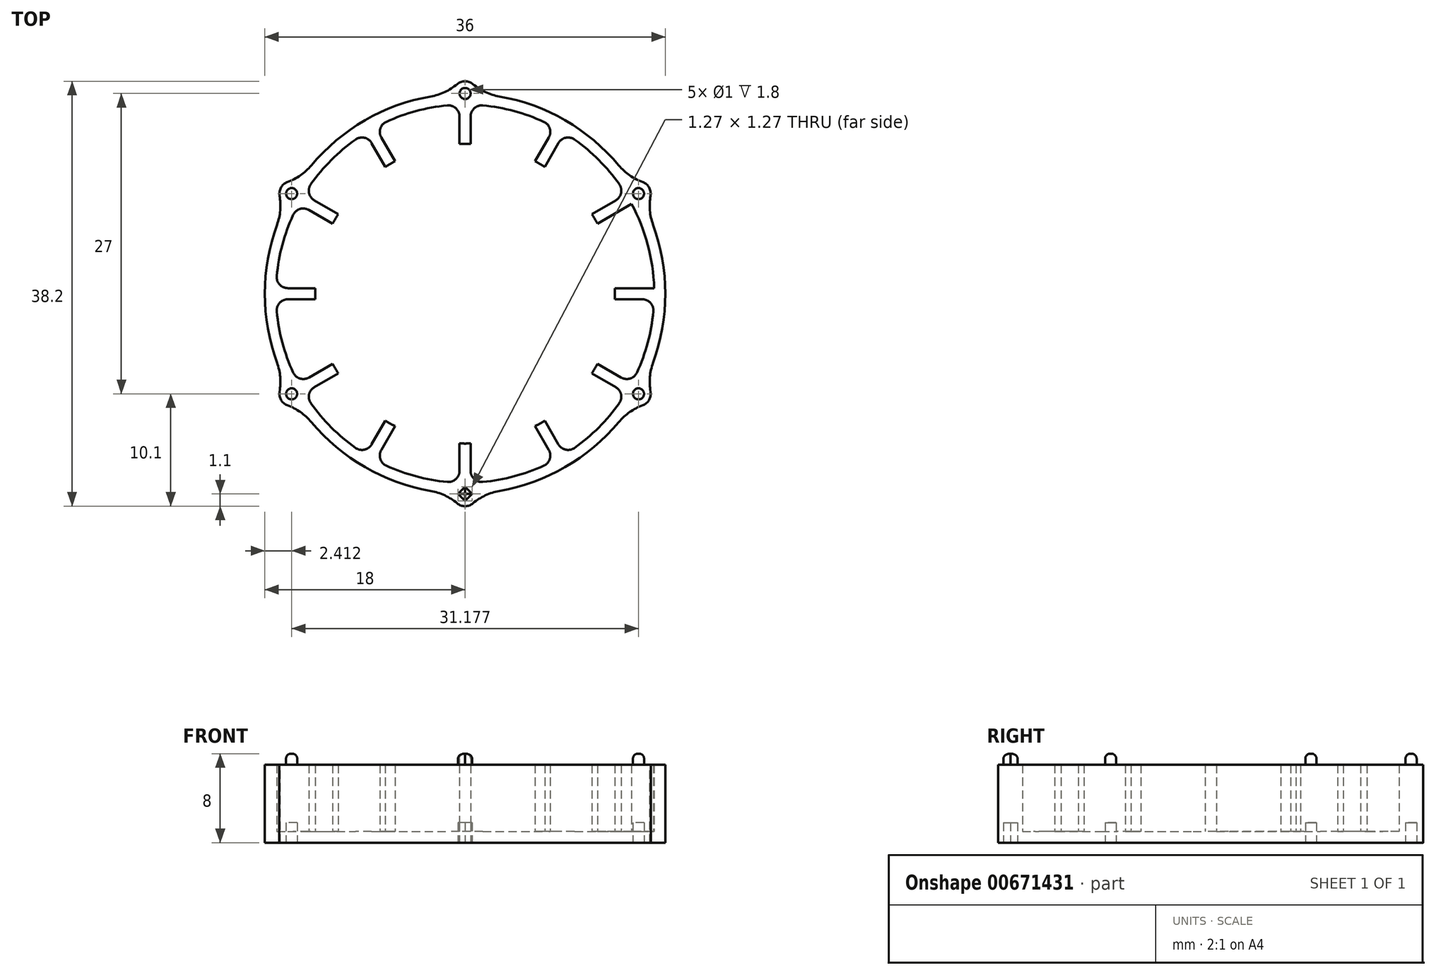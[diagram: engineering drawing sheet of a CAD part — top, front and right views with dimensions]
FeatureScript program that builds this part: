
annotation { "Feature Type Name" : "Feature", "Feature Type Description" : "" }
export const myFeature = defineFeature(function(context is Context, id is Id, definition is map)
    precondition{}
    {
        {
            var Q0;
            Q0=qCreatedBy(makeId("Top.planeOp"),FACE);
            var sketch = newSketch(context, id + "F0", { "sketchPlane" : qUnion([Q0])});
            skCircle(sketch, "E0", {"center": v(0, 0) * mm, "radius": 18 * mm});
            skCircle(sketch, "E1.0", {"center": v(0, 0) * mm, "radius": 17 * mm});
            skLineSegment(sketch, "E2.bottom", {"start": v(8.56, 15.83) * mm, "end": v(9.43, 15.33) * mm});
            skLineSegment(sketch, "E2.top", {"start": v(-9.43, -15.33) * mm, "end": v(-8.56, -15.83) * mm});
            skLineSegment(sketch, "E2.left", {"start": v(8.56, 15.83) * mm, "end": v(-9.43, -15.33) * mm});
            skLineSegment(sketch, "E2.right", {"start": v(9.43, 15.33) * mm, "end": v(-8.56, -15.83) * mm});
            skLineSegment(sketch, "E3.bottom", {"start": v(15.33, 9.43) * mm, "end": v(15.83, 8.56) * mm});
            skLineSegment(sketch, "E3.top", {"start": v(-15.83, -8.56) * mm, "end": v(-15.33, -9.43) * mm});
            skLineSegment(sketch, "E3.left", {"start": v(15.33, 9.43) * mm, "end": v(-15.83, -8.56) * mm});
            skLineSegment(sketch, "E3.right", {"start": v(15.83, 8.56) * mm, "end": v(-15.33, -9.43) * mm});
            skLineSegment(sketch, "E4", {"start": v(-38.35, 0) * mm, "end": v(39.17, 0) * mm, "construction": true});
            skLineSegment(sketch, "E5", {"start": v(0, 42.5) * mm, "end": v(0, -42.47) * mm, "construction": true});
            skLineSegment(sketch, "E6.bottom", {"start": v(-18, 0.5) * mm, "end": v(18, 0.5) * mm});
            skLineSegment(sketch, "E6.top", {"start": v(-18, -0.5) * mm, "end": v(18, -0.5) * mm});
            skLineSegment(sketch, "E6.left", {"start": v(-18, 0.5) * mm, "end": v(-18, -0.5) * mm});
            skLineSegment(sketch, "E6.right", {"start": v(18, 0.5) * mm, "end": v(18, -0.5) * mm});
            skLineSegment(sketch, "E7.bottom", {"start": v(-15.33, 9.43) * mm, "end": v(15.83, -8.56) * mm});
            skLineSegment(sketch, "E7.top", {"start": v(-15.83, 8.56) * mm, "end": v(15.33, -9.43) * mm});
            skLineSegment(sketch, "E7.left", {"start": v(-15.33, 9.43) * mm, "end": v(-15.83, 8.56) * mm});
            skLineSegment(sketch, "E7.right", {"start": v(15.83, -8.56) * mm, "end": v(15.33, -9.43) * mm});
            skLineSegment(sketch, "E8.bottom", {"start": v(-0.5, 18) * mm, "end": v(0.5, 18) * mm});
            skLineSegment(sketch, "E8.top", {"start": v(-0.5, -18) * mm, "end": v(0.5, -18) * mm});
            skLineSegment(sketch, "E8.left", {"start": v(-0.5, 18) * mm, "end": v(-0.5, -18) * mm});
            skLineSegment(sketch, "E8.right", {"start": v(0.5, 18) * mm, "end": v(0.5, -18) * mm});
            skLineSegment(sketch, "E9.bottom", {"start": v(-9.43, 15.33) * mm, "end": v(-8.56, 15.83) * mm});
            skLineSegment(sketch, "E9.top", {"start": v(8.56, -15.83) * mm, "end": v(9.43, -15.33) * mm});
            skLineSegment(sketch, "E9.left", {"start": v(-9.43, 15.33) * mm, "end": v(8.56, -15.83) * mm});
            skLineSegment(sketch, "E9.right", {"start": v(-8.56, 15.83) * mm, "end": v(9.43, -15.33) * mm});
            skCircle(sketch, "E10", {"center": v(0, 0) * mm, "radius": 13.47 * mm});
            skSolve(sketch);
        }
        {
            var Q0;
            Q0=qCreatedBy(makeId("Top.planeOp"),FACE);
            var sketch = newSketch(context, id + "F1", { "sketchPlane" : qUnion([Q0])});
            skCircle(sketch, "E11", {"center": v(0, 0) * mm, "radius": 18 * mm});
            skCircle(sketch, "E12", {"center": v(0, 0) * mm, "radius": 17 * mm});
            skSolve(sketch);
        }
        {
            var Q0;
            Q0=makeQuery(id+"F1.imprint","IMPRINT",FACE,{"disambiguationData":[TD([[makeQuery(id+"F1.imprint","IMPRINT",EDGE,{"derivedFrom":sQuery(id+"F1.wireOp",EDGE,"E11")}),1.0]])]});
            extrude(context, id + "F2", {"entities" : qUnion([Q0]), "depth" : 7 * mm, "offsetDistance" : 25 * mm});
        }
        {
            var Q0;
            {var subQ0=sQuery(id+"F0.wireOp",EDGE,"E7.bottom");var subQ1=sQuery(id+"F0.wireOp",EDGE,"E1.0");var subQ2=makeQuery(id+"F0.imprint","INTERSECT",VERTEX,{"disambiguationData":[OD(0.0)],"derivedFrom":[subQ1,subQ0]});Q0=makeQuery(id+"F0.imprint","IMPRINT",FACE,{"disambiguationData":[TD([[makeQuery(id+"F0.imprint","IMPRINT",EDGE,{"disambiguationData":[TD([[subQ2,-1.0]])],"derivedFrom":subQ1}),1.0]])]});}
            var Q1;
            {var subQ0=sQuery(id+"F0.wireOp",EDGE,"E2.right");var subQ1=sQuery(id+"F0.wireOp",EDGE,"E1.0");var subQ2=makeQuery(id+"F0.imprint","INTERSECT",VERTEX,{"disambiguationData":[OD(0.0)],"derivedFrom":[subQ1,subQ0]});Q1=makeQuery(id+"F0.imprint","IMPRINT",FACE,{"disambiguationData":[TD([[makeQuery(id+"F0.imprint","IMPRINT",EDGE,{"disambiguationData":[TD([[subQ2,-1.0]])],"derivedFrom":subQ1}),1.0]])]});}
            var Q2;
            {var subQ0=sQuery(id+"F0.wireOp",EDGE,"E6.bottom");var subQ1=sQuery(id+"F0.wireOp",EDGE,"E1.0");var subQ2=makeQuery(id+"F0.imprint","INTERSECT",VERTEX,{"disambiguationData":[OD(0.0)],"derivedFrom":[subQ1,subQ0]});Q2=makeQuery(id+"F0.imprint","IMPRINT",FACE,{"disambiguationData":[TD([[makeQuery(id+"F0.imprint","IMPRINT",EDGE,{"disambiguationData":[TD([[subQ2,1.0]])],"derivedFrom":subQ1}),1.0]])]});}
            var Q3;
            {var subQ0=sQuery(id+"F0.wireOp",EDGE,"E8.left");var subQ1=sQuery(id+"F0.wireOp",EDGE,"E1.0");var subQ2=makeQuery(id+"F0.imprint","INTERSECT",VERTEX,{"disambiguationData":[OD(1.0)],"derivedFrom":[subQ1,subQ0]});Q3=makeQuery(id+"F0.imprint","IMPRINT",FACE,{"disambiguationData":[TD([[makeQuery(id+"F0.imprint","IMPRINT",EDGE,{"disambiguationData":[TD([[subQ2,-1.0]])],"derivedFrom":subQ1}),1.0]])]});}
            var Q4;
            {var subQ0=sQuery(id+"F0.wireOp",EDGE,"E3.left");var subQ1=sQuery(id+"F0.wireOp",EDGE,"E1.0");var subQ2=makeQuery(id+"F0.imprint","INTERSECT",VERTEX,{"disambiguationData":[OD(1.0)],"derivedFrom":[subQ1,subQ0]});Q4=makeQuery(id+"F0.imprint","IMPRINT",FACE,{"disambiguationData":[TD([[makeQuery(id+"F0.imprint","IMPRINT",EDGE,{"disambiguationData":[TD([[subQ2,-1.0]])],"derivedFrom":subQ1}),1.0]])]});}
            var Q5;
            {var subQ0=sQuery(id+"F0.wireOp",EDGE,"E9.right");var subQ1=sQuery(id+"F0.wireOp",EDGE,"E1.0");var subQ2=makeQuery(id+"F0.imprint","INTERSECT",VERTEX,{"disambiguationData":[OD(0.0)],"derivedFrom":[subQ1,subQ0]});Q5=makeQuery(id+"F0.imprint","IMPRINT",FACE,{"disambiguationData":[TD([[makeQuery(id+"F0.imprint","IMPRINT",EDGE,{"disambiguationData":[TD([[subQ2,-1.0]])],"derivedFrom":subQ1}),1.0]])]});}
            var Q6;
            {var subQ0=sQuery(id+"F0.wireOp",EDGE,"E8.right");var subQ1=sQuery(id+"F0.wireOp",EDGE,"E1.0");var subQ2=makeQuery(id+"F0.imprint","INTERSECT",VERTEX,{"disambiguationData":[OD(0.0)],"derivedFrom":[subQ1,subQ0]});Q6=makeQuery(id+"F0.imprint","IMPRINT",FACE,{"disambiguationData":[TD([[makeQuery(id+"F0.imprint","IMPRINT",EDGE,{"disambiguationData":[TD([[subQ2,-1.0]])],"derivedFrom":subQ1}),1.0]])]});}
            var Q7;
            {var subQ0=sQuery(id+"F0.wireOp",EDGE,"E3.right");var subQ1=sQuery(id+"F0.wireOp",EDGE,"E1.0");var subQ2=makeQuery(id+"F0.imprint","INTERSECT",VERTEX,{"disambiguationData":[OD(0.0)],"derivedFrom":[subQ1,subQ0]});Q7=makeQuery(id+"F0.imprint","IMPRINT",FACE,{"disambiguationData":[TD([[makeQuery(id+"F0.imprint","IMPRINT",EDGE,{"disambiguationData":[TD([[subQ2,-1.0]])],"derivedFrom":subQ1}),1.0]])]});}
            var Q8;
            {var subQ0=sQuery(id+"F0.wireOp",EDGE,"E7.top");var subQ1=sQuery(id+"F0.wireOp",EDGE,"E1.0");var subQ2=makeQuery(id+"F0.imprint","INTERSECT",VERTEX,{"disambiguationData":[OD(1.0)],"derivedFrom":[subQ1,subQ0]});Q8=makeQuery(id+"F0.imprint","IMPRINT",FACE,{"disambiguationData":[TD([[makeQuery(id+"F0.imprint","IMPRINT",EDGE,{"disambiguationData":[TD([[subQ2,-1.0]])],"derivedFrom":subQ1}),1.0]])]});}
            var Q9;
            {var subQ0=sQuery(id+"F0.wireOp",EDGE,"E9.left");var subQ1=sQuery(id+"F0.wireOp",EDGE,"E1.0");var subQ2=makeQuery(id+"F0.imprint","INTERSECT",VERTEX,{"disambiguationData":[OD(1.0)],"derivedFrom":[subQ1,subQ0]});Q9=makeQuery(id+"F0.imprint","IMPRINT",FACE,{"disambiguationData":[TD([[makeQuery(id+"F0.imprint","IMPRINT",EDGE,{"disambiguationData":[TD([[subQ2,-1.0]])],"derivedFrom":subQ1}),1.0]])]});}
            var Q10;
            {var subQ0=sQuery(id+"F0.wireOp",EDGE,"E2.left");var subQ1=sQuery(id+"F0.wireOp",EDGE,"E1.0");var subQ2=makeQuery(id+"F0.imprint","INTERSECT",VERTEX,{"disambiguationData":[OD(1.0)],"derivedFrom":[subQ1,subQ0]});Q10=makeQuery(id+"F0.imprint","IMPRINT",FACE,{"disambiguationData":[TD([[makeQuery(id+"F0.imprint","IMPRINT",EDGE,{"disambiguationData":[TD([[subQ2,-1.0]])],"derivedFrom":subQ1}),1.0]])]});}
            var Q11;
            {var subQ0=sQuery(id+"F0.wireOp",EDGE,"E6.bottom");var subQ1=sQuery(id+"F0.wireOp",EDGE,"E1.0");var subQ2=makeQuery(id+"F0.imprint","INTERSECT",VERTEX,{"disambiguationData":[OD(1.0)],"derivedFrom":[subQ1,subQ0]});Q11=makeQuery(id+"F0.imprint","IMPRINT",FACE,{"disambiguationData":[TD([[makeQuery(id+"F0.imprint","IMPRINT",EDGE,{"disambiguationData":[TD([[subQ2,-1.0]])],"derivedFrom":subQ1}),1.0]])]});}
            extrude(context, id + "F3", {"entities" : qUnion([Q0, Q1, Q2, Q3, Q4, Q5, Q6, Q7, Q8, Q9, Q10, Q11]), "operationType" : NewBodyOperationType.ADD, "depth" : 7 * mm, "offsetDistance" : 25 * mm});
        }
        {
            var Q0;
            Q0=makeQuery(id+"F1.imprint","IMPRINT",FACE,{"disambiguationData":[TD([[makeQuery(id+"F1.imprint","IMPRINT",EDGE,{"derivedFrom":sQuery(id+"F1.wireOp",EDGE,"E11")}),1.0]])]});
            var Q1;
            Q1=makeQuery(id+"F1.imprint","IMPRINT",FACE,{"disambiguationData":[TD([[makeQuery(id+"F1.imprint","IMPRINT",EDGE,{"derivedFrom":sQuery(id+"F1.wireOp",EDGE,"E12")}),1.0]])]});
            extrude(context, id + "F4", {"entities" : qUnion([Q0, Q1]), "operationType" : NewBodyOperationType.ADD, "depth" : 1 * mm, "offsetDistance" : 25 * mm});
        }
        {
            var Q0;
            Q0=qCreatedBy(makeId("Top.planeOp"),FACE);
            var sketch = newSketch(context, id + "F5", { "sketchPlane" : qUnion([Q0])});
            skCircle(sketch, "E13", {"center": v(0, 0) * mm, "radius": 18 * mm});
            skLineSegment(sketch, "E14", {"start": v(0, 18) * mm, "end": v(0, -18) * mm, "construction": true});
            skLineSegment(sketch, "E15", {"start": v(15.59, 9) * mm, "end": v(0, 0) * mm, "construction": true});
            skLineSegment(sketch, "E16", {"start": v(9, 15.59) * mm, "end": v(0, 0) * mm, "construction": true});
            skLineSegment(sketch, "E17", {"start": v(0, 0) * mm, "end": v(18, 0) * mm, "construction": true});
            skLineSegment(sketch, "E18", {"start": v(0, 0) * mm, "end": v(15.59, -9) * mm, "construction": true});
            skLineSegment(sketch, "E19", {"start": v(0, 0) * mm, "end": v(9, -15.59) * mm, "construction": true});
            skLineSegment(sketch, "E20", {"start": v(0, 0) * mm, "end": v(-9, 15.59) * mm, "construction": true});
            skLineSegment(sketch, "E21", {"start": v(0, 0) * mm, "end": v(-15.59, 9) * mm, "construction": true});
            skLineSegment(sketch, "E22", {"start": v(0, 0) * mm, "end": v(-18, 0) * mm, "construction": true});
            skLineSegment(sketch, "E23", {"start": v(0, 0) * mm, "end": v(-15.59, -9) * mm, "construction": true});
            skLineSegment(sketch, "E24", {"start": v(0, 0) * mm, "end": v(-9, -15.59) * mm, "construction": true});
            skCircle(sketch, "E25", {"center": v(0, 18) * mm, "radius": 1.1 * mm});
            skCircle(sketch, "E26", {"center": v(15.59, 9) * mm, "radius": 1.1 * mm});
            skCircle(sketch, "E27", {"center": v(15.59, -9) * mm, "radius": 1.1 * mm});
            skCircle(sketch, "E28", {"center": v(0, -18) * mm, "radius": 1.1 * mm});
            skCircle(sketch, "E29", {"center": v(-15.59, -9) * mm, "radius": 1.1 * mm});
            skCircle(sketch, "E30", {"center": v(-15.59, 9) * mm, "radius": 1.1 * mm});
            skCircle(sketch, "E31", {"center": v(-15.59, 9) * mm, "radius": 0.5 * mm});
            skCircle(sketch, "E32", {"center": v(0, 18) * mm, "radius": 0.5 * mm});
            skCircle(sketch, "E33", {"center": v(15.59, 9) * mm, "radius": 0.5 * mm});
            skCircle(sketch, "E34", {"center": v(15.59, -9) * mm, "radius": 0.5 * mm});
            skCircle(sketch, "E35", {"center": v(-15.59, -9) * mm, "radius": 0.5 * mm});
            skLineSegment(sketch, "E36.bottom", {"start": v(0.64, -18) * mm, "end": v(0, -18.64) * mm});
            skLineSegment(sketch, "E36.top", {"start": v(0, -17.36) * mm, "end": v(-0.64, -18) * mm});
            skLineSegment(sketch, "E36.left", {"start": v(0.64, -18) * mm, "end": v(0, -17.36) * mm});
            skLineSegment(sketch, "E36.right", {"start": v(0, -18.64) * mm, "end": v(-0.64, -18) * mm});
            skSolve(sketch);
        }
        {
            var Q0;
            {var subQ0=sQuery(id+"F5.wireOp",EDGE,"E30");var subQ1=sQuery(id+"F5.wireOp",EDGE,"E13");var subQ2=makeQuery(id+"F5.imprint","INTERSECT",VERTEX,{"disambiguationData":[OD(0.0)],"derivedFrom":[subQ1,subQ0]});Q0=makeQuery(id+"F5.imprint","IMPRINT",FACE,{"disambiguationData":[TD([[makeQuery(id+"F5.imprint","IMPRINT",EDGE,{"disambiguationData":[TD([[subQ2,-1.0]])],"derivedFrom":subQ1}),1.0]])]});}
            var Q1;
            {var subQ0=sQuery(id+"F5.wireOp",EDGE,"E30");var subQ1=sQuery(id+"F5.wireOp",EDGE,"E13");var subQ2=makeQuery(id+"F5.imprint","INTERSECT",VERTEX,{"disambiguationData":[OD(0.0)],"derivedFrom":[subQ1,subQ0]});Q1=makeQuery(id+"F5.imprint","IMPRINT",FACE,{"disambiguationData":[TD([[makeQuery(id+"F5.imprint","IMPRINT",EDGE,{"disambiguationData":[TD([[subQ2,-1.0]])],"derivedFrom":subQ1}),-1.0]])]});}
            var Q2;
            {var subQ0=sQuery(id+"F5.wireOp",EDGE,"E25");var subQ1=sQuery(id+"F5.wireOp",EDGE,"E13");var subQ2=makeQuery(id+"F5.imprint","INTERSECT",VERTEX,{"disambiguationData":[OD(0.0)],"derivedFrom":[subQ1,subQ0]});Q2=makeQuery(id+"F5.imprint","IMPRINT",FACE,{"disambiguationData":[TD([[makeQuery(id+"F5.imprint","IMPRINT",EDGE,{"disambiguationData":[TD([[subQ2,-1.0]])],"derivedFrom":subQ1}),1.0]])]});}
            var Q3;
            {var subQ0=sQuery(id+"F5.wireOp",EDGE,"E25");var subQ1=sQuery(id+"F5.wireOp",EDGE,"E13");var subQ2=makeQuery(id+"F5.imprint","INTERSECT",VERTEX,{"disambiguationData":[OD(0.0)],"derivedFrom":[subQ1,subQ0]});Q3=makeQuery(id+"F5.imprint","IMPRINT",FACE,{"disambiguationData":[TD([[makeQuery(id+"F5.imprint","IMPRINT",EDGE,{"disambiguationData":[TD([[subQ2,-1.0]])],"derivedFrom":subQ1}),-1.0]])]});}
            var Q4;
            {var subQ0=sQuery(id+"F5.wireOp",EDGE,"E26");var subQ1=sQuery(id+"F5.wireOp",EDGE,"E13");var subQ2=makeQuery(id+"F5.imprint","INTERSECT",VERTEX,{"disambiguationData":[OD(0.0)],"derivedFrom":[subQ1,subQ0]});Q4=makeQuery(id+"F5.imprint","IMPRINT",FACE,{"disambiguationData":[TD([[makeQuery(id+"F5.imprint","IMPRINT",EDGE,{"disambiguationData":[TD([[subQ2,-1.0]])],"derivedFrom":subQ1}),-1.0]])]});}
            var Q5;
            {var subQ0=sQuery(id+"F5.wireOp",EDGE,"E26");var subQ1=sQuery(id+"F5.wireOp",EDGE,"E13");var subQ2=makeQuery(id+"F5.imprint","INTERSECT",VERTEX,{"disambiguationData":[OD(0.0)],"derivedFrom":[subQ1,subQ0]});Q5=makeQuery(id+"F5.imprint","IMPRINT",FACE,{"disambiguationData":[TD([[makeQuery(id+"F5.imprint","IMPRINT",EDGE,{"disambiguationData":[TD([[subQ2,-1.0]])],"derivedFrom":subQ1}),1.0]])]});}
            var Q6;
            {var subQ0=sQuery(id+"F5.wireOp",EDGE,"E29");var subQ1=sQuery(id+"F5.wireOp",EDGE,"E13");var subQ2=makeQuery(id+"F5.imprint","INTERSECT",VERTEX,{"disambiguationData":[OD(0.0)],"derivedFrom":[subQ1,subQ0]});Q6=makeQuery(id+"F5.imprint","IMPRINT",FACE,{"disambiguationData":[TD([[makeQuery(id+"F5.imprint","IMPRINT",EDGE,{"disambiguationData":[TD([[subQ2,-1.0]])],"derivedFrom":subQ1}),1.0]])]});}
            var Q7;
            {var subQ0=sQuery(id+"F5.wireOp",EDGE,"E29");var subQ1=sQuery(id+"F5.wireOp",EDGE,"E13");var subQ2=makeQuery(id+"F5.imprint","INTERSECT",VERTEX,{"disambiguationData":[OD(0.0)],"derivedFrom":[subQ1,subQ0]});Q7=makeQuery(id+"F5.imprint","IMPRINT",FACE,{"disambiguationData":[TD([[makeQuery(id+"F5.imprint","IMPRINT",EDGE,{"disambiguationData":[TD([[subQ2,-1.0]])],"derivedFrom":subQ1}),-1.0]])]});}
            var Q8;
            {var subQ3=sQuery(id+"F5.wireOp",EDGE,"E13");var subQ5=sQuery(id+"F5.wireOp",EDGE,"E28");var subQ6=makeQuery(id+"F5.imprint","INTERSECT",VERTEX,{"disambiguationData":[OD(0.0)],"derivedFrom":[subQ3,subQ5]});Q8=makeQuery(id+"F5.imprint","IMPRINT",FACE,{"disambiguationData":[TD([[makeQuery(id+"F5.imprint","IMPRINT",EDGE,{"disambiguationData":[TD([[subQ6,-1.0]])],"derivedFrom":subQ3}),1.0]])]});}
            var Q9;
            {var subQ6=sQuery(id+"F5.wireOp",EDGE,"E36.bottom");Q9=makeQuery(id+"F5.imprint","IMPRINT",FACE,{"disambiguationData":[TD([[makeQuery(id+"F5.imprint","IMPRINT",EDGE,{"derivedFrom":subQ6}),1.0]])]});}
            var Q10;
            {var subQ0=sQuery(id+"F5.wireOp",EDGE,"E27");var subQ1=sQuery(id+"F5.wireOp",EDGE,"E13");var subQ2=makeQuery(id+"F5.imprint","INTERSECT",VERTEX,{"disambiguationData":[OD(0.0)],"derivedFrom":[subQ1,subQ0]});Q10=makeQuery(id+"F5.imprint","IMPRINT",FACE,{"disambiguationData":[TD([[makeQuery(id+"F5.imprint","IMPRINT",EDGE,{"disambiguationData":[TD([[subQ2,-1.0]])],"derivedFrom":subQ1}),-1.0]])]});}
            var Q11;
            {var subQ0=sQuery(id+"F5.wireOp",EDGE,"E27");var subQ1=sQuery(id+"F5.wireOp",EDGE,"E13");var subQ2=makeQuery(id+"F5.imprint","INTERSECT",VERTEX,{"disambiguationData":[OD(0.0)],"derivedFrom":[subQ1,subQ0]});Q11=makeQuery(id+"F5.imprint","IMPRINT",FACE,{"disambiguationData":[TD([[makeQuery(id+"F5.imprint","IMPRINT",EDGE,{"disambiguationData":[TD([[subQ2,-1.0]])],"derivedFrom":subQ1}),1.0]])]});}
            var Q12;
            {var subQ0=sQuery(id+"F5.wireOp",EDGE,"E31");var subQ1=sQuery(id+"F5.wireOp",EDGE,"E13");var subQ2=makeQuery(id+"F5.imprint","INTERSECT",VERTEX,{"disambiguationData":[OD(0.0)],"derivedFrom":[subQ1,subQ0]});Q12=makeQuery(id+"F5.imprint","IMPRINT",FACE,{"disambiguationData":[TD([[makeQuery(id+"F5.imprint","IMPRINT",EDGE,{"disambiguationData":[TD([[subQ2,-1.0]])],"derivedFrom":subQ1}),1.0]])]});}
            var Q13;
            {var subQ0=sQuery(id+"F5.wireOp",EDGE,"E31");var subQ1=sQuery(id+"F5.wireOp",EDGE,"E13");var subQ2=makeQuery(id+"F5.imprint","INTERSECT",VERTEX,{"disambiguationData":[OD(0.0)],"derivedFrom":[subQ1,subQ0]});Q13=makeQuery(id+"F5.imprint","IMPRINT",FACE,{"disambiguationData":[TD([[makeQuery(id+"F5.imprint","IMPRINT",EDGE,{"disambiguationData":[TD([[subQ2,-1.0]])],"derivedFrom":subQ1}),-1.0]])]});}
            var Q14;
            {var subQ0=sQuery(id+"F5.wireOp",EDGE,"E32");var subQ1=sQuery(id+"F5.wireOp",EDGE,"E13");var subQ2=makeQuery(id+"F5.imprint","INTERSECT",VERTEX,{"disambiguationData":[OD(0.0)],"derivedFrom":[subQ1,subQ0]});Q14=makeQuery(id+"F5.imprint","IMPRINT",FACE,{"disambiguationData":[TD([[makeQuery(id+"F5.imprint","IMPRINT",EDGE,{"disambiguationData":[TD([[subQ2,-1.0]])],"derivedFrom":subQ1}),-1.0]])]});}
            var Q15;
            {var subQ0=sQuery(id+"F5.wireOp",EDGE,"E32");var subQ1=sQuery(id+"F5.wireOp",EDGE,"E13");var subQ2=makeQuery(id+"F5.imprint","INTERSECT",VERTEX,{"disambiguationData":[OD(0.0)],"derivedFrom":[subQ1,subQ0]});Q15=makeQuery(id+"F5.imprint","IMPRINT",FACE,{"disambiguationData":[TD([[makeQuery(id+"F5.imprint","IMPRINT",EDGE,{"disambiguationData":[TD([[subQ2,-1.0]])],"derivedFrom":subQ1}),1.0]])]});}
            var Q16;
            {var subQ0=sQuery(id+"F5.wireOp",EDGE,"E33");var subQ1=sQuery(id+"F5.wireOp",EDGE,"E13");var subQ2=makeQuery(id+"F5.imprint","INTERSECT",VERTEX,{"disambiguationData":[OD(0.0)],"derivedFrom":[subQ1,subQ0]});Q16=makeQuery(id+"F5.imprint","IMPRINT",FACE,{"disambiguationData":[TD([[makeQuery(id+"F5.imprint","IMPRINT",EDGE,{"disambiguationData":[TD([[subQ2,-1.0]])],"derivedFrom":subQ1}),-1.0]])]});}
            var Q17;
            {var subQ0=sQuery(id+"F5.wireOp",EDGE,"E33");var subQ1=sQuery(id+"F5.wireOp",EDGE,"E13");var subQ2=makeQuery(id+"F5.imprint","INTERSECT",VERTEX,{"disambiguationData":[OD(0.0)],"derivedFrom":[subQ1,subQ0]});Q17=makeQuery(id+"F5.imprint","IMPRINT",FACE,{"disambiguationData":[TD([[makeQuery(id+"F5.imprint","IMPRINT",EDGE,{"disambiguationData":[TD([[subQ2,-1.0]])],"derivedFrom":subQ1}),1.0]])]});}
            var Q18;
            {var subQ0=sQuery(id+"F5.wireOp",EDGE,"E34");var subQ1=sQuery(id+"F5.wireOp",EDGE,"E13");var subQ2=makeQuery(id+"F5.imprint","INTERSECT",VERTEX,{"disambiguationData":[OD(0.0)],"derivedFrom":[subQ1,subQ0]});Q18=makeQuery(id+"F5.imprint","IMPRINT",FACE,{"disambiguationData":[TD([[makeQuery(id+"F5.imprint","IMPRINT",EDGE,{"disambiguationData":[TD([[subQ2,-1.0]])],"derivedFrom":subQ1}),-1.0]])]});}
            var Q19;
            {var subQ0=sQuery(id+"F5.wireOp",EDGE,"E34");var subQ1=sQuery(id+"F5.wireOp",EDGE,"E13");var subQ2=makeQuery(id+"F5.imprint","INTERSECT",VERTEX,{"disambiguationData":[OD(0.0)],"derivedFrom":[subQ1,subQ0]});Q19=makeQuery(id+"F5.imprint","IMPRINT",FACE,{"disambiguationData":[TD([[makeQuery(id+"F5.imprint","IMPRINT",EDGE,{"disambiguationData":[TD([[subQ2,-1.0]])],"derivedFrom":subQ1}),1.0]])]});}
            var Q20;
            {var subQ1=sQuery(id+"F5.wireOp",EDGE,"E36.bottom");Q20=makeQuery(id+"F5.imprint","IMPRINT",FACE,{"disambiguationData":[TD([[makeQuery(id+"F5.imprint","IMPRINT",EDGE,{"derivedFrom":subQ1}),-1.0]])]});}
            var Q21;
            {var subQ0=sQuery(id+"F5.wireOp",EDGE,"E35");var subQ1=sQuery(id+"F5.wireOp",EDGE,"E13");var subQ2=makeQuery(id+"F5.imprint","INTERSECT",VERTEX,{"disambiguationData":[OD(0.0)],"derivedFrom":[subQ1,subQ0]});Q21=makeQuery(id+"F5.imprint","IMPRINT",FACE,{"disambiguationData":[TD([[makeQuery(id+"F5.imprint","IMPRINT",EDGE,{"disambiguationData":[TD([[subQ2,-1.0]])],"derivedFrom":subQ1}),-1.0]])]});}
            var Q22;
            {var subQ0=sQuery(id+"F5.wireOp",EDGE,"E35");var subQ1=sQuery(id+"F5.wireOp",EDGE,"E13");var subQ2=makeQuery(id+"F5.imprint","INTERSECT",VERTEX,{"disambiguationData":[OD(0.0)],"derivedFrom":[subQ1,subQ0]});Q22=makeQuery(id+"F5.imprint","IMPRINT",FACE,{"disambiguationData":[TD([[makeQuery(id+"F5.imprint","IMPRINT",EDGE,{"disambiguationData":[TD([[subQ2,-1.0]])],"derivedFrom":subQ1}),1.0]])]});}
            var Q23;
            {var subQ0=sQuery(id+"F5.wireOp",EDGE,"E36.top");var subQ1=sQuery(id+"F5.wireOp",EDGE,"E13");var subQ2=makeQuery(id+"F5.imprint","INTERSECT",VERTEX,{"derivedFrom":[subQ1,subQ0]});Q23=makeQuery(id+"F5.imprint","IMPRINT",FACE,{"disambiguationData":[TD([[makeQuery(id+"F5.imprint","IMPRINT",EDGE,{"disambiguationData":[TD([[subQ2,-1.0]])],"derivedFrom":subQ1}),1.0]])]});}
            extrude(context, id + "F6", {"entities" : qUnion([Q0, Q1, Q2, Q3, Q4, Q5, Q6, Q7, Q8, Q9, Q10, Q11, Q12, Q13, Q14, Q15, Q16, Q17, Q18, Q19, Q20, Q21, Q22, Q23]), "operationType" : NewBodyOperationType.ADD, "depth" : 7 * mm, "offsetDistance" : 25 * mm});
        }
        {
            var Q0;
            {var subQ0=sQuery(id+"F0.wireOp",EDGE,"E8.right");var subQ1=sQuery(id+"F0.wireOp",EDGE,"E1.0");Q0=makeQuery(id+"F3.opExtrude","SWEPT_EDGE",EDGE,{"disambiguationData":[OSD([subQ1,subQ0]),TDD([makeQuery(id+"F0.imprint","INTERSECT",VERTEX,{"disambiguationData":[OD(1.0)],"derivedFrom":[subQ1,subQ0]})])]});}
            var Q1;
            {var subQ0=sQuery(id+"F0.wireOp",EDGE,"E2.left");var subQ1=sQuery(id+"F0.wireOp",EDGE,"E1.0");Q1=makeQuery(id+"F3.opExtrude","SWEPT_EDGE",EDGE,{"disambiguationData":[OSD([subQ1,subQ0]),TDD([makeQuery(id+"F0.imprint","INTERSECT",VERTEX,{"disambiguationData":[OD(1.0)],"derivedFrom":[subQ1,subQ0]})])]});}
            var Q2;
            {var subQ0=sQuery(id+"F0.wireOp",EDGE,"E3.left");var subQ1=sQuery(id+"F0.wireOp",EDGE,"E1.0");Q2=makeQuery(id+"F3.opExtrude","SWEPT_EDGE",EDGE,{"disambiguationData":[OSD([subQ1,subQ0]),TDD([makeQuery(id+"F0.imprint","INTERSECT",VERTEX,{"disambiguationData":[OD(1.0)],"derivedFrom":[subQ1,subQ0]})])]});}
            var Q3;
            {var subQ0=sQuery(id+"F0.wireOp",EDGE,"E6.bottom");var subQ1=sQuery(id+"F0.wireOp",EDGE,"E1.0");Q3=makeQuery(id+"F3.opExtrude","SWEPT_EDGE",EDGE,{"disambiguationData":[OSD([subQ1,subQ0]),TDD([makeQuery(id+"F0.imprint","INTERSECT",VERTEX,{"disambiguationData":[OD(1.0)],"derivedFrom":[subQ1,subQ0]})])]});}
            var Q4;
            {var subQ0=sQuery(id+"F0.wireOp",EDGE,"E9.right");var subQ1=sQuery(id+"F0.wireOp",EDGE,"E1.0");Q4=makeQuery(id+"F3.opExtrude","SWEPT_EDGE",EDGE,{"disambiguationData":[OSD([subQ1,subQ0]),TDD([makeQuery(id+"F0.imprint","INTERSECT",VERTEX,{"disambiguationData":[OD(1.0)],"derivedFrom":[subQ1,subQ0]})])]});}
            var Q5;
            {var subQ0=sQuery(id+"F0.wireOp",EDGE,"E7.bottom");var subQ1=sQuery(id+"F0.wireOp",EDGE,"E1.0");Q5=makeQuery(id+"F3.opExtrude","SWEPT_EDGE",EDGE,{"disambiguationData":[OSD([subQ1,subQ0]),TDD([makeQuery(id+"F0.imprint","INTERSECT",VERTEX,{"disambiguationData":[OD(1.0)],"derivedFrom":[subQ1,subQ0]})])]});}
            var Q6;
            {var subQ0=sQuery(id+"F0.wireOp",EDGE,"E8.left");var subQ1=sQuery(id+"F0.wireOp",EDGE,"E1.0");Q6=makeQuery(id+"F3.opExtrude","SWEPT_EDGE",EDGE,{"disambiguationData":[OSD([subQ1,subQ0]),TDD([makeQuery(id+"F0.imprint","INTERSECT",VERTEX,{"disambiguationData":[OD(0.0)],"derivedFrom":[subQ1,subQ0]})])]});}
            var Q7;
            {var subQ0=sQuery(id+"F0.wireOp",EDGE,"E2.left");var subQ1=sQuery(id+"F0.wireOp",EDGE,"E1.0");Q7=makeQuery(id+"F3.opExtrude","SWEPT_EDGE",EDGE,{"disambiguationData":[OSD([subQ1,subQ0]),TDD([makeQuery(id+"F0.imprint","INTERSECT",VERTEX,{"disambiguationData":[OD(0.0)],"derivedFrom":[subQ1,subQ0]})])]});}
            var Q8;
            {var subQ0=sQuery(id+"F0.wireOp",EDGE,"E3.left");var subQ1=sQuery(id+"F0.wireOp",EDGE,"E1.0");Q8=makeQuery(id+"F3.opExtrude","SWEPT_EDGE",EDGE,{"disambiguationData":[OSD([subQ1,subQ0]),TDD([makeQuery(id+"F0.imprint","INTERSECT",VERTEX,{"disambiguationData":[OD(0.0)],"derivedFrom":[subQ1,subQ0]})])]});}
            var Q9;
            {var subQ0=sQuery(id+"F0.wireOp",EDGE,"E6.top");var subQ1=sQuery(id+"F0.wireOp",EDGE,"E1.0");Q9=makeQuery(id+"F3.opExtrude","SWEPT_EDGE",EDGE,{"disambiguationData":[OSD([subQ1,subQ0]),TDD([makeQuery(id+"F0.imprint","INTERSECT",VERTEX,{"disambiguationData":[OD(1.0)],"derivedFrom":[subQ1,subQ0]})])]});}
            var Q10;
            {var subQ0=sQuery(id+"F0.wireOp",EDGE,"E7.top");var subQ1=sQuery(id+"F0.wireOp",EDGE,"E1.0");Q10=makeQuery(id+"F3.opExtrude","SWEPT_EDGE",EDGE,{"disambiguationData":[OSD([subQ1,subQ0]),TDD([makeQuery(id+"F0.imprint","INTERSECT",VERTEX,{"disambiguationData":[OD(0.0)],"derivedFrom":[subQ1,subQ0]})])]});}
            var Q11;
            {var subQ0=sQuery(id+"F0.wireOp",EDGE,"E6.top");var subQ1=sQuery(id+"F0.wireOp",EDGE,"E1.0");Q11=makeQuery(id+"F3.opExtrude","SWEPT_EDGE",EDGE,{"disambiguationData":[OSD([subQ1,subQ0]),TDD([makeQuery(id+"F0.imprint","INTERSECT",VERTEX,{"disambiguationData":[OD(0.0)],"derivedFrom":[subQ1,subQ0]})])]});}
            var Q12;
            {var subQ0=sQuery(id+"F0.wireOp",EDGE,"E9.left");var subQ1=sQuery(id+"F0.wireOp",EDGE,"E1.0");Q12=makeQuery(id+"F3.opExtrude","SWEPT_EDGE",EDGE,{"disambiguationData":[OSD([subQ1,subQ0]),TDD([makeQuery(id+"F0.imprint","INTERSECT",VERTEX,{"disambiguationData":[OD(0.0)],"derivedFrom":[subQ1,subQ0]})])]});}
            var Q13;
            {var subQ0=sQuery(id+"F0.wireOp",EDGE,"E8.right");var subQ1=sQuery(id+"F0.wireOp",EDGE,"E1.0");Q13=makeQuery(id+"F3.opExtrude","SWEPT_EDGE",EDGE,{"disambiguationData":[OSD([subQ1,subQ0]),TDD([makeQuery(id+"F0.imprint","INTERSECT",VERTEX,{"disambiguationData":[OD(0.0)],"derivedFrom":[subQ1,subQ0]})])]});}
            var Q14;
            {var subQ0=sQuery(id+"F0.wireOp",EDGE,"E7.bottom");var subQ1=sQuery(id+"F0.wireOp",EDGE,"E1.0");Q14=makeQuery(id+"F3.opExtrude","SWEPT_EDGE",EDGE,{"disambiguationData":[OSD([subQ1,subQ0]),TDD([makeQuery(id+"F0.imprint","INTERSECT",VERTEX,{"disambiguationData":[OD(0.0)],"derivedFrom":[subQ1,subQ0]})])]});}
            var Q15;
            {var subQ0=sQuery(id+"F0.wireOp",EDGE,"E9.right");var subQ1=sQuery(id+"F0.wireOp",EDGE,"E1.0");Q15=makeQuery(id+"F3.opExtrude","SWEPT_EDGE",EDGE,{"disambiguationData":[OSD([subQ1,subQ0]),TDD([makeQuery(id+"F0.imprint","INTERSECT",VERTEX,{"disambiguationData":[OD(0.0)],"derivedFrom":[subQ1,subQ0]})])]});}
            var Q16;
            {var subQ0=sQuery(id+"F0.wireOp",EDGE,"E3.right");var subQ1=sQuery(id+"F0.wireOp",EDGE,"E1.0");Q16=makeQuery(id+"F3.opExtrude","SWEPT_EDGE",EDGE,{"disambiguationData":[OSD([subQ1,subQ0]),TDD([makeQuery(id+"F0.imprint","INTERSECT",VERTEX,{"disambiguationData":[OD(1.0)],"derivedFrom":[subQ1,subQ0]})])]});}
            var Q17;
            {var subQ0=sQuery(id+"F0.wireOp",EDGE,"E2.right");var subQ1=sQuery(id+"F0.wireOp",EDGE,"E1.0");Q17=makeQuery(id+"F3.opExtrude","SWEPT_EDGE",EDGE,{"disambiguationData":[OSD([subQ1,subQ0]),TDD([makeQuery(id+"F0.imprint","INTERSECT",VERTEX,{"disambiguationData":[OD(1.0)],"derivedFrom":[subQ1,subQ0]})])]});}
            var Q18;
            {var subQ0=sQuery(id+"F0.wireOp",EDGE,"E3.right");var subQ1=sQuery(id+"F0.wireOp",EDGE,"E1.0");Q18=makeQuery(id+"F3.opExtrude","SWEPT_EDGE",EDGE,{"disambiguationData":[OSD([subQ1,subQ0]),TDD([makeQuery(id+"F0.imprint","INTERSECT",VERTEX,{"disambiguationData":[OD(0.0)],"derivedFrom":[subQ1,subQ0]})])]});}
            var Q19;
            {var subQ0=sQuery(id+"F0.wireOp",EDGE,"E2.right");var subQ1=sQuery(id+"F0.wireOp",EDGE,"E1.0");Q19=makeQuery(id+"F3.opExtrude","SWEPT_EDGE",EDGE,{"disambiguationData":[OSD([subQ1,subQ0]),TDD([makeQuery(id+"F0.imprint","INTERSECT",VERTEX,{"disambiguationData":[OD(0.0)],"derivedFrom":[subQ1,subQ0]})])]});}
            var Q20;
            {var subQ0=sQuery(id+"F0.wireOp",EDGE,"E8.left");var subQ1=sQuery(id+"F0.wireOp",EDGE,"E1.0");Q20=makeQuery(id+"F3.opExtrude","SWEPT_EDGE",EDGE,{"disambiguationData":[OSD([subQ1,subQ0]),TDD([makeQuery(id+"F0.imprint","INTERSECT",VERTEX,{"disambiguationData":[OD(1.0)],"derivedFrom":[subQ1,subQ0]})])]});}
            var Q21;
            {var subQ0=sQuery(id+"F0.wireOp",EDGE,"E9.left");var subQ1=sQuery(id+"F0.wireOp",EDGE,"E1.0");Q21=makeQuery(id+"F3.opExtrude","SWEPT_EDGE",EDGE,{"disambiguationData":[OSD([subQ1,subQ0]),TDD([makeQuery(id+"F0.imprint","INTERSECT",VERTEX,{"disambiguationData":[OD(1.0)],"derivedFrom":[subQ1,subQ0]})])]});}
            var Q22;
            {var subQ0=sQuery(id+"F0.wireOp",EDGE,"E7.top");var subQ1=sQuery(id+"F0.wireOp",EDGE,"E1.0");Q22=makeQuery(id+"F3.opExtrude","SWEPT_EDGE",EDGE,{"disambiguationData":[OSD([subQ1,subQ0]),TDD([makeQuery(id+"F0.imprint","INTERSECT",VERTEX,{"disambiguationData":[OD(1.0)],"derivedFrom":[subQ1,subQ0]})])]});}
            var Q23;
            {var subQ0=sQuery(id+"F0.wireOp",EDGE,"E6.bottom");var subQ1=sQuery(id+"F0.wireOp",EDGE,"E1.0");Q23=makeQuery(id+"F3.opExtrude","SWEPT_EDGE",EDGE,{"disambiguationData":[OSD([subQ1,subQ0]),TDD([makeQuery(id+"F0.imprint","INTERSECT",VERTEX,{"disambiguationData":[OD(0.0)],"derivedFrom":[subQ1,subQ0]})])]});}
            fillet(context, id + "F7", {"entities" : qUnion([Q0, Q1, Q2, Q3, Q4, Q5, Q6, Q7, Q8, Q9, Q10, Q11, Q12, Q13, Q14, Q15, Q16, Q17, Q18, Q19, Q20, Q21, Q22, Q23]), "radius" : 1 * mm, "tangentPropagation" : true, "allowEdgeOverflow" : false});
        }
        {
            var Q0;
            Q0=makeQuery(id+"F6.boolean.opBoolean","INTERSECT",EDGE,{"disambiguationData":[OD(0.0)],"derivedFrom":[makeQuery(id+"F2.opExtrude","SWEPT_FACE",FACE,{"disambiguationData":[OSD([sQuery(id+"F1.wireOp",EDGE,"E11")])]}),makeQuery(id+"F6.opExtrude","SWEPT_FACE",FACE,{"disambiguationData":[OSD([sQuery(id+"F5.wireOp",EDGE,"E30")])]})]});
            var Q1;
            Q1=makeQuery(id+"F6.boolean.opBoolean","INTERSECT",EDGE,{"disambiguationData":[OD(1.0)],"derivedFrom":[makeQuery(id+"F2.opExtrude","SWEPT_FACE",FACE,{"disambiguationData":[OSD([sQuery(id+"F1.wireOp",EDGE,"E11")])]}),makeQuery(id+"F6.opExtrude","SWEPT_FACE",FACE,{"disambiguationData":[OSD([sQuery(id+"F5.wireOp",EDGE,"E30")])]})]});
            var Q2;
            Q2=makeQuery(id+"F6.boolean.opBoolean","INTERSECT",EDGE,{"disambiguationData":[OD(1.0)],"derivedFrom":[makeQuery(id+"F2.opExtrude","SWEPT_FACE",FACE,{"disambiguationData":[OSD([sQuery(id+"F1.wireOp",EDGE,"E11")])]}),makeQuery(id+"F6.opExtrude","SWEPT_FACE",FACE,{"disambiguationData":[OSD([sQuery(id+"F5.wireOp",EDGE,"E25")])]})]});
            var Q3;
            Q3=makeQuery(id+"F6.boolean.opBoolean","INTERSECT",EDGE,{"disambiguationData":[OD(1.0)],"derivedFrom":[makeQuery(id+"F2.opExtrude","SWEPT_FACE",FACE,{"disambiguationData":[OSD([sQuery(id+"F1.wireOp",EDGE,"E11")])]}),makeQuery(id+"F6.opExtrude","SWEPT_FACE",FACE,{"disambiguationData":[OSD([sQuery(id+"F5.wireOp",EDGE,"E29")])]})]});
            var Q4;
            Q4=makeQuery(id+"F6.boolean.opBoolean","INTERSECT",EDGE,{"disambiguationData":[OD(0.0)],"derivedFrom":[makeQuery(id+"F2.opExtrude","SWEPT_FACE",FACE,{"disambiguationData":[OSD([sQuery(id+"F1.wireOp",EDGE,"E11")])]}),makeQuery(id+"F6.opExtrude","SWEPT_FACE",FACE,{"disambiguationData":[OSD([sQuery(id+"F5.wireOp",EDGE,"E29")])]})]});
            var Q5;
            Q5=makeQuery(id+"F6.boolean.opBoolean","INTERSECT",EDGE,{"disambiguationData":[OD(1.0)],"derivedFrom":[makeQuery(id+"F2.opExtrude","SWEPT_FACE",FACE,{"disambiguationData":[OSD([sQuery(id+"F1.wireOp",EDGE,"E11")])]}),makeQuery(id+"F6.opExtrude","SWEPT_FACE",FACE,{"disambiguationData":[OSD([sQuery(id+"F5.wireOp",EDGE,"E28")])]})]});
            var Q6;
            Q6=makeQuery(id+"F6.boolean.opBoolean","INTERSECT",EDGE,{"disambiguationData":[OD(0.0)],"derivedFrom":[makeQuery(id+"F2.opExtrude","SWEPT_FACE",FACE,{"disambiguationData":[OSD([sQuery(id+"F1.wireOp",EDGE,"E11")])]}),makeQuery(id+"F6.opExtrude","SWEPT_FACE",FACE,{"disambiguationData":[OSD([sQuery(id+"F5.wireOp",EDGE,"E28")])]})]});
            var Q7;
            Q7=makeQuery(id+"F6.boolean.opBoolean","INTERSECT",EDGE,{"disambiguationData":[OD(1.0)],"derivedFrom":[makeQuery(id+"F2.opExtrude","SWEPT_FACE",FACE,{"disambiguationData":[OSD([sQuery(id+"F1.wireOp",EDGE,"E11")])]}),makeQuery(id+"F6.opExtrude","SWEPT_FACE",FACE,{"disambiguationData":[OSD([sQuery(id+"F5.wireOp",EDGE,"E27")])]})]});
            var Q8;
            Q8=makeQuery(id+"F6.boolean.opBoolean","INTERSECT",EDGE,{"disambiguationData":[OD(0.0)],"derivedFrom":[makeQuery(id+"F2.opExtrude","SWEPT_FACE",FACE,{"disambiguationData":[OSD([sQuery(id+"F1.wireOp",EDGE,"E11")])]}),makeQuery(id+"F6.opExtrude","SWEPT_FACE",FACE,{"disambiguationData":[OSD([sQuery(id+"F5.wireOp",EDGE,"E27")])]})]});
            var Q9;
            Q9=makeQuery(id+"F6.boolean.opBoolean","INTERSECT",EDGE,{"disambiguationData":[OD(1.0)],"derivedFrom":[makeQuery(id+"F2.opExtrude","SWEPT_FACE",FACE,{"disambiguationData":[OSD([sQuery(id+"F1.wireOp",EDGE,"E11")])]}),makeQuery(id+"F6.opExtrude","SWEPT_FACE",FACE,{"disambiguationData":[OSD([sQuery(id+"F5.wireOp",EDGE,"E26")])]})]});
            var Q10;
            Q10=makeQuery(id+"F6.boolean.opBoolean","INTERSECT",EDGE,{"disambiguationData":[OD(0.0)],"derivedFrom":[makeQuery(id+"F2.opExtrude","SWEPT_FACE",FACE,{"disambiguationData":[OSD([sQuery(id+"F1.wireOp",EDGE,"E11")])]}),makeQuery(id+"F6.opExtrude","SWEPT_FACE",FACE,{"disambiguationData":[OSD([sQuery(id+"F5.wireOp",EDGE,"E26")])]})]});
            var Q11;
            Q11=makeQuery(id+"F6.boolean.opBoolean","INTERSECT",EDGE,{"disambiguationData":[OD(0.0)],"derivedFrom":[makeQuery(id+"F2.opExtrude","SWEPT_FACE",FACE,{"disambiguationData":[OSD([sQuery(id+"F1.wireOp",EDGE,"E11")])]}),makeQuery(id+"F6.opExtrude","SWEPT_FACE",FACE,{"disambiguationData":[OSD([sQuery(id+"F5.wireOp",EDGE,"E25")])]})]});
            fillet(context, id + "F8", {"entities" : qUnion([Q0, Q1, Q2, Q3, Q4, Q5, Q6, Q7, Q8, Q9, Q10, Q11]), "radius" : 5 * mm, "tangentPropagation" : true, "allowEdgeOverflow" : false});
        }
        {
            var Q0;
            {var subQ0=sQuery(id+"F5.wireOp",EDGE,"E31");var subQ1=sQuery(id+"F5.wireOp",EDGE,"E13");var subQ2=makeQuery(id+"F5.imprint","INTERSECT",VERTEX,{"disambiguationData":[OD(0.0)],"derivedFrom":[subQ1,subQ0]});Q0=makeQuery(id+"F5.imprint","IMPRINT",FACE,{"disambiguationData":[TD([[makeQuery(id+"F5.imprint","IMPRINT",EDGE,{"disambiguationData":[TD([[subQ2,-1.0]])],"derivedFrom":subQ1}),-1.0]])]});}
            var Q1;
            {var subQ0=sQuery(id+"F5.wireOp",EDGE,"E31");var subQ1=sQuery(id+"F5.wireOp",EDGE,"E13");var subQ2=makeQuery(id+"F5.imprint","INTERSECT",VERTEX,{"disambiguationData":[OD(0.0)],"derivedFrom":[subQ1,subQ0]});Q1=makeQuery(id+"F5.imprint","IMPRINT",FACE,{"disambiguationData":[TD([[makeQuery(id+"F5.imprint","IMPRINT",EDGE,{"disambiguationData":[TD([[subQ2,-1.0]])],"derivedFrom":subQ1}),1.0]])]});}
            var Q2;
            {var subQ0=sQuery(id+"F5.wireOp",EDGE,"E32");var subQ1=sQuery(id+"F5.wireOp",EDGE,"E13");var subQ2=makeQuery(id+"F5.imprint","INTERSECT",VERTEX,{"disambiguationData":[OD(0.0)],"derivedFrom":[subQ1,subQ0]});Q2=makeQuery(id+"F5.imprint","IMPRINT",FACE,{"disambiguationData":[TD([[makeQuery(id+"F5.imprint","IMPRINT",EDGE,{"disambiguationData":[TD([[subQ2,-1.0]])],"derivedFrom":subQ1}),-1.0]])]});}
            var Q3;
            {var subQ0=sQuery(id+"F5.wireOp",EDGE,"E32");var subQ1=sQuery(id+"F5.wireOp",EDGE,"E13");var subQ2=makeQuery(id+"F5.imprint","INTERSECT",VERTEX,{"disambiguationData":[OD(0.0)],"derivedFrom":[subQ1,subQ0]});Q3=makeQuery(id+"F5.imprint","IMPRINT",FACE,{"disambiguationData":[TD([[makeQuery(id+"F5.imprint","IMPRINT",EDGE,{"disambiguationData":[TD([[subQ2,-1.0]])],"derivedFrom":subQ1}),1.0]])]});}
            var Q4;
            {var subQ0=sQuery(id+"F5.wireOp",EDGE,"E33");var subQ1=sQuery(id+"F5.wireOp",EDGE,"E13");var subQ2=makeQuery(id+"F5.imprint","INTERSECT",VERTEX,{"disambiguationData":[OD(0.0)],"derivedFrom":[subQ1,subQ0]});Q4=makeQuery(id+"F5.imprint","IMPRINT",FACE,{"disambiguationData":[TD([[makeQuery(id+"F5.imprint","IMPRINT",EDGE,{"disambiguationData":[TD([[subQ2,-1.0]])],"derivedFrom":subQ1}),1.0]])]});}
            var Q5;
            {var subQ0=sQuery(id+"F5.wireOp",EDGE,"E33");var subQ1=sQuery(id+"F5.wireOp",EDGE,"E13");var subQ2=makeQuery(id+"F5.imprint","INTERSECT",VERTEX,{"disambiguationData":[OD(0.0)],"derivedFrom":[subQ1,subQ0]});Q5=makeQuery(id+"F5.imprint","IMPRINT",FACE,{"disambiguationData":[TD([[makeQuery(id+"F5.imprint","IMPRINT",EDGE,{"disambiguationData":[TD([[subQ2,-1.0]])],"derivedFrom":subQ1}),-1.0]])]});}
            var Q6;
            {var subQ0=sQuery(id+"F5.wireOp",EDGE,"E34");var subQ1=sQuery(id+"F5.wireOp",EDGE,"E13");var subQ2=makeQuery(id+"F5.imprint","INTERSECT",VERTEX,{"disambiguationData":[OD(0.0)],"derivedFrom":[subQ1,subQ0]});Q6=makeQuery(id+"F5.imprint","IMPRINT",FACE,{"disambiguationData":[TD([[makeQuery(id+"F5.imprint","IMPRINT",EDGE,{"disambiguationData":[TD([[subQ2,-1.0]])],"derivedFrom":subQ1}),1.0]])]});}
            var Q7;
            {var subQ0=sQuery(id+"F5.wireOp",EDGE,"E34");var subQ1=sQuery(id+"F5.wireOp",EDGE,"E13");var subQ2=makeQuery(id+"F5.imprint","INTERSECT",VERTEX,{"disambiguationData":[OD(0.0)],"derivedFrom":[subQ1,subQ0]});Q7=makeQuery(id+"F5.imprint","IMPRINT",FACE,{"disambiguationData":[TD([[makeQuery(id+"F5.imprint","IMPRINT",EDGE,{"disambiguationData":[TD([[subQ2,-1.0]])],"derivedFrom":subQ1}),-1.0]])]});}
            var Q8;
            {var subQ1=sQuery(id+"F5.wireOp",EDGE,"E36.bottom");Q8=makeQuery(id+"F5.imprint","IMPRINT",FACE,{"disambiguationData":[TD([[makeQuery(id+"F5.imprint","IMPRINT",EDGE,{"derivedFrom":subQ1}),-1.0]])]});}
            var Q9;
            {var subQ0=sQuery(id+"F5.wireOp",EDGE,"E36.top");var subQ1=sQuery(id+"F5.wireOp",EDGE,"E13");var subQ2=makeQuery(id+"F5.imprint","INTERSECT",VERTEX,{"derivedFrom":[subQ1,subQ0]});Q9=makeQuery(id+"F5.imprint","IMPRINT",FACE,{"disambiguationData":[TD([[makeQuery(id+"F5.imprint","IMPRINT",EDGE,{"disambiguationData":[TD([[subQ2,-1.0]])],"derivedFrom":subQ1}),1.0]])]});}
            var Q10;
            {var subQ0=sQuery(id+"F5.wireOp",EDGE,"E35");var subQ1=sQuery(id+"F5.wireOp",EDGE,"E13");var subQ2=makeQuery(id+"F5.imprint","INTERSECT",VERTEX,{"disambiguationData":[OD(0.0)],"derivedFrom":[subQ1,subQ0]});Q10=makeQuery(id+"F5.imprint","IMPRINT",FACE,{"disambiguationData":[TD([[makeQuery(id+"F5.imprint","IMPRINT",EDGE,{"disambiguationData":[TD([[subQ2,-1.0]])],"derivedFrom":subQ1}),-1.0]])]});}
            var Q11;
            {var subQ0=sQuery(id+"F5.wireOp",EDGE,"E35");var subQ1=sQuery(id+"F5.wireOp",EDGE,"E13");var subQ2=makeQuery(id+"F5.imprint","INTERSECT",VERTEX,{"disambiguationData":[OD(0.0)],"derivedFrom":[subQ1,subQ0]});Q11=makeQuery(id+"F5.imprint","IMPRINT",FACE,{"disambiguationData":[TD([[makeQuery(id+"F5.imprint","IMPRINT",EDGE,{"disambiguationData":[TD([[subQ2,-1.0]])],"derivedFrom":subQ1}),1.0]])]});}
            extrude(context, id + "F9", {"entities" : qUnion([Q0, Q1, Q2, Q3, Q4, Q5, Q6, Q7, Q8, Q9, Q10, Q11]), "operationType" : NewBodyOperationType.ADD, "depth" : 8 * mm, "offsetDistance" : 25 * mm});
        }
        {
            var Q0;
            Q0=makeQuery(id+"F9.opExtrude","CAP_EDGE",EDGE,{"disambiguationData":[OSD([sQuery(id+"F5.wireOp",EDGE,"E35")])],"isStart":false});
            var Q1;
            Q1=makeQuery(id+"F9.opExtrude","CAP_FACE",FACE,{"disambiguationData":[OSD([sQuery(id+"F5.wireOp",EDGE,"E31")])],"isStart":false});
            var Q2;
            Q2=makeQuery(id+"F9.opExtrude","CAP_FACE",FACE,{"disambiguationData":[OSD([sQuery(id+"F5.wireOp",EDGE,"E32")])],"isStart":false});
            var Q3;
            Q3=makeQuery(id+"F9.opExtrude","CAP_FACE",FACE,{"disambiguationData":[OSD([sQuery(id+"F5.wireOp",EDGE,"E33")])],"isStart":false});
            var Q4;
            Q4=makeQuery(id+"F9.opExtrude","CAP_FACE",FACE,{"disambiguationData":[OSD([sQuery(id+"F5.wireOp",EDGE,"E34")])],"isStart":false});
            var Q5;
            Q5=makeQuery(id+"F9.opExtrude","CAP_EDGE",EDGE,{"disambiguationData":[OSD([sQuery(id+"F5.wireOp",EDGE,"E36.left")])],"isStart":false});
            var Q6;
            Q6=makeQuery(id+"F9.opExtrude","CAP_EDGE",EDGE,{"disambiguationData":[OSD([sQuery(id+"F5.wireOp",EDGE,"E36.right")])],"isStart":false});
            var Q7;
            Q7=makeQuery(id+"F9.opExtrude","CAP_EDGE",EDGE,{"disambiguationData":[OSD([sQuery(id+"F5.wireOp",EDGE,"E36.bottom")])],"isStart":false});
            var Q8;
            Q8=makeQuery(id+"F9.opExtrude","CAP_EDGE",EDGE,{"disambiguationData":[OSD([sQuery(id+"F5.wireOp",EDGE,"E36.top")])],"isStart":false});
            fillet(context, id + "F10", {"entities" : qUnion([Q0, Q1, Q2, Q3, Q4, Q5, Q6, Q7, Q8]), "radius" : .45 * mm, "tangentPropagation" : true, "allowEdgeOverflow" : false});
        }
        {
            var Q0;
            {var subQ0=sQuery(id+"F5.wireOp",EDGE,"E35");var subQ1=sQuery(id+"F5.wireOp",EDGE,"E13");var subQ2=makeQuery(id+"F5.imprint","INTERSECT",VERTEX,{"disambiguationData":[OD(0.0)],"derivedFrom":[subQ1,subQ0]});Q0=makeQuery(id+"F5.imprint","IMPRINT",FACE,{"disambiguationData":[TD([[makeQuery(id+"F5.imprint","IMPRINT",EDGE,{"disambiguationData":[TD([[subQ2,-1.0]])],"derivedFrom":subQ1}),-1.0]])]});}
            var Q1;
            {var subQ0=sQuery(id+"F5.wireOp",EDGE,"E35");var subQ1=sQuery(id+"F5.wireOp",EDGE,"E13");var subQ2=makeQuery(id+"F5.imprint","INTERSECT",VERTEX,{"disambiguationData":[OD(0.0)],"derivedFrom":[subQ1,subQ0]});Q1=makeQuery(id+"F5.imprint","IMPRINT",FACE,{"disambiguationData":[TD([[makeQuery(id+"F5.imprint","IMPRINT",EDGE,{"disambiguationData":[TD([[subQ2,-1.0]])],"derivedFrom":subQ1}),1.0]])]});}
            var Q2;
            {var subQ1=sQuery(id+"F5.wireOp",EDGE,"E36.bottom");Q2=makeQuery(id+"F5.imprint","IMPRINT",FACE,{"disambiguationData":[TD([[makeQuery(id+"F5.imprint","IMPRINT",EDGE,{"derivedFrom":subQ1}),-1.0]])]});}
            var Q3;
            {var subQ0=sQuery(id+"F5.wireOp",EDGE,"E36.top");var subQ1=sQuery(id+"F5.wireOp",EDGE,"E13");var subQ2=makeQuery(id+"F5.imprint","INTERSECT",VERTEX,{"derivedFrom":[subQ1,subQ0]});Q3=makeQuery(id+"F5.imprint","IMPRINT",FACE,{"disambiguationData":[TD([[makeQuery(id+"F5.imprint","IMPRINT",EDGE,{"disambiguationData":[TD([[subQ2,-1.0]])],"derivedFrom":subQ1}),1.0]])]});}
            var Q4;
            {var subQ0=sQuery(id+"F5.wireOp",EDGE,"E34");var subQ1=sQuery(id+"F5.wireOp",EDGE,"E13");var subQ2=makeQuery(id+"F5.imprint","INTERSECT",VERTEX,{"disambiguationData":[OD(0.0)],"derivedFrom":[subQ1,subQ0]});Q4=makeQuery(id+"F5.imprint","IMPRINT",FACE,{"disambiguationData":[TD([[makeQuery(id+"F5.imprint","IMPRINT",EDGE,{"disambiguationData":[TD([[subQ2,-1.0]])],"derivedFrom":subQ1}),1.0]])]});}
            var Q5;
            {var subQ0=sQuery(id+"F5.wireOp",EDGE,"E34");var subQ1=sQuery(id+"F5.wireOp",EDGE,"E13");var subQ2=makeQuery(id+"F5.imprint","INTERSECT",VERTEX,{"disambiguationData":[OD(0.0)],"derivedFrom":[subQ1,subQ0]});Q5=makeQuery(id+"F5.imprint","IMPRINT",FACE,{"disambiguationData":[TD([[makeQuery(id+"F5.imprint","IMPRINT",EDGE,{"disambiguationData":[TD([[subQ2,-1.0]])],"derivedFrom":subQ1}),-1.0]])]});}
            var Q6;
            {var subQ0=sQuery(id+"F5.wireOp",EDGE,"E33");var subQ1=sQuery(id+"F5.wireOp",EDGE,"E13");var subQ2=makeQuery(id+"F5.imprint","INTERSECT",VERTEX,{"disambiguationData":[OD(0.0)],"derivedFrom":[subQ1,subQ0]});Q6=makeQuery(id+"F5.imprint","IMPRINT",FACE,{"disambiguationData":[TD([[makeQuery(id+"F5.imprint","IMPRINT",EDGE,{"disambiguationData":[TD([[subQ2,-1.0]])],"derivedFrom":subQ1}),1.0]])]});}
            var Q7;
            {var subQ0=sQuery(id+"F5.wireOp",EDGE,"E33");var subQ1=sQuery(id+"F5.wireOp",EDGE,"E13");var subQ2=makeQuery(id+"F5.imprint","INTERSECT",VERTEX,{"disambiguationData":[OD(0.0)],"derivedFrom":[subQ1,subQ0]});Q7=makeQuery(id+"F5.imprint","IMPRINT",FACE,{"disambiguationData":[TD([[makeQuery(id+"F5.imprint","IMPRINT",EDGE,{"disambiguationData":[TD([[subQ2,-1.0]])],"derivedFrom":subQ1}),-1.0]])]});}
            var Q8;
            {var subQ0=sQuery(id+"F5.wireOp",EDGE,"E32");var subQ1=sQuery(id+"F5.wireOp",EDGE,"E13");var subQ2=makeQuery(id+"F5.imprint","INTERSECT",VERTEX,{"disambiguationData":[OD(0.0)],"derivedFrom":[subQ1,subQ0]});Q8=makeQuery(id+"F5.imprint","IMPRINT",FACE,{"disambiguationData":[TD([[makeQuery(id+"F5.imprint","IMPRINT",EDGE,{"disambiguationData":[TD([[subQ2,-1.0]])],"derivedFrom":subQ1}),1.0]])]});}
            var Q9;
            {var subQ0=sQuery(id+"F5.wireOp",EDGE,"E32");var subQ1=sQuery(id+"F5.wireOp",EDGE,"E13");var subQ2=makeQuery(id+"F5.imprint","INTERSECT",VERTEX,{"disambiguationData":[OD(0.0)],"derivedFrom":[subQ1,subQ0]});Q9=makeQuery(id+"F5.imprint","IMPRINT",FACE,{"disambiguationData":[TD([[makeQuery(id+"F5.imprint","IMPRINT",EDGE,{"disambiguationData":[TD([[subQ2,-1.0]])],"derivedFrom":subQ1}),-1.0]])]});}
            var Q10;
            {var subQ0=sQuery(id+"F5.wireOp",EDGE,"E31");var subQ1=sQuery(id+"F5.wireOp",EDGE,"E13");var subQ2=makeQuery(id+"F5.imprint","INTERSECT",VERTEX,{"disambiguationData":[OD(0.0)],"derivedFrom":[subQ1,subQ0]});Q10=makeQuery(id+"F5.imprint","IMPRINT",FACE,{"disambiguationData":[TD([[makeQuery(id+"F5.imprint","IMPRINT",EDGE,{"disambiguationData":[TD([[subQ2,-1.0]])],"derivedFrom":subQ1}),-1.0]])]});}
            var Q11;
            {var subQ0=sQuery(id+"F5.wireOp",EDGE,"E31");var subQ1=sQuery(id+"F5.wireOp",EDGE,"E13");var subQ2=makeQuery(id+"F5.imprint","INTERSECT",VERTEX,{"disambiguationData":[OD(0.0)],"derivedFrom":[subQ1,subQ0]});Q11=makeQuery(id+"F5.imprint","IMPRINT",FACE,{"disambiguationData":[TD([[makeQuery(id+"F5.imprint","IMPRINT",EDGE,{"disambiguationData":[TD([[subQ2,-1.0]])],"derivedFrom":subQ1}),1.0]])]});}
            extrude(context, id + "F11", {"entities" : qUnion([Q0, Q1, Q2, Q3, Q4, Q5, Q6, Q7, Q8, Q9, Q10, Q11]), "operationType" : NewBodyOperationType.REMOVE, "depth" : 1.8 * mm, "offsetDistance" : 25 * mm});
        }
    });
